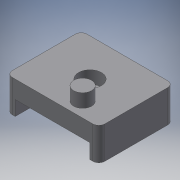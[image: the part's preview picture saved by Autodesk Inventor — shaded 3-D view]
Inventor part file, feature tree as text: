
AUTODESK INVENTOR PART (.ipt)
format: ipt  version: 2019 (Build 230136000, 136)  size: 142,336 bytes
history: native  units: in
note: dims shown in document units (in); Inventor stores cm internally (conversion verified against a paired STEP export)
features: sketch x5, extrude x4, hole x1, fillet x1
ambient origin geometry x8: Origin, YZ Plane, XZ Plane, XY Plane, X Axis, Y Axis, Z Axis, Center Point
bodies: Solid1 (feature_tree)
feature tree (11):
  extrude  "Extrusion1"  Depth=1.2362in
  hole  "Hole1"  [1 undecoded]
  extrude  "Extrusion2"  Depth=0.168in
  extrude  "Extrusion3"  Depth=0.1969in
  extrude  "Extrusion4"  Depth=0.0787in
  fillet  "Fillet1"  Radius=1.0in
  sketch  "Sketch1"  dims[d0=1.0in d1=1.2362in]
  sketch  "Sketch2"  dims[d2=0.2362in d3=0.0in]
  sketch  "Sketch3"  dims[d4=0.177in d5=0.2362in d6=0.332in d7=0.0787in d8=0.5635in d9=0.315in d10=0.8108in d11=0.3051in]
  sketch  "Sketch4"  dims[d12=0.168in d13=0.0in d14=0.24in]
  sketch  "Sketch5"  dims[d15=0.18in d16=0.0in d18=0.1969in d19=0.0787in d20=1.0in d21=0.1969in d22=0.0in d23=0.4134in]
note: 1 required parameter value undecoded (feature->parameter linkage not recoverable at this tier; creation-order binding heuristic only, values carry confidence <= 0.55)
